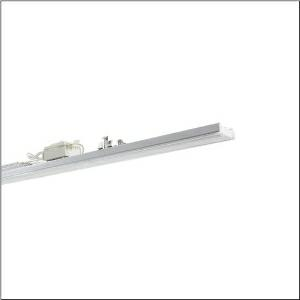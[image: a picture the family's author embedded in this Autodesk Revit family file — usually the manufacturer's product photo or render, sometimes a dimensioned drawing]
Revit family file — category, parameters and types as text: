
# Revit family: licross_11_recessed_ho_51tl12dn4exm
name_source: partatom
category: Lighting Fixtures
units: mm (PartAtom-declared; Revit-internal decimal feet)

## family parameters
Cut with Voids When Loaded = No
Host = Face
Light Source = No
Part Type = Normal
Room Calculation Point = No
Round Connector Dimension = Use Diameter
Shared = No

## types (1)
- --- (1 x LED, 14030 lm, 76.8 W, 4000K)
    Apparent Load = 77 VA
    CIE Flux Codes = 66 91 98 100 100
    Color Rendering = 80
    Color Temperature = 4000K
    Default Elevation = 1800 mm
    Description = Licross 11 Recessed HO, luminaire insert, of sheet steel, coil coated, white, length: 1.500mm, width: 66mm, height: 67mm, LED rated luminous flux: 14.030lm, light colour: 840, SDCM (Standard Deviation of Colour Matching)MacAdam ≤ 2 SDCM (initial), control gear: DALI 2, with plug, 5-pole, with phase selection, mains connection: 220..240V, AC, 50/60Hz, rated input power: 77W, internal wiring halogen-free, primary optical cover: cover, of PMMA, light emission: direct distribution, primary light characteristic: symmetric, protection rating (complete): IP40, insulation class (complete): insulation class I (protective earthing), certification: CE, ENEC, VDE, UKCA, protection symbol: D if used in an environment without relevant dust loads with corresponding accessories, impact resistance: IK06, permissible ambient temperature for indoor applications: -25..+30°C, corresponds to IFS (International Featured Standards) requirements for safety and quality in the food industry, reducing of maximum allowable ambient temperature of 5°C with ceiling mounting, LABS conformity tested according to VDMA 24364:2018-05, The light source and the operating device comply with the requirements of the Ecodesign Regulation (EU) 2019/2020 and are replaceable in accordance with this regulation, packaging unit: 1 piece
    Height = 58 mm
    Lamp = 1 x LED
    Lamp Light Flux = 14030 lm
    Lamp Power = 76.8 W
    Lamp count = 1
    Length = 1500 mm
    Luminous efficacy = 183 lm/W
    Manufacturer = Siteco
    ModVariant = No
    Model = 51TL12DN4EXM
    Mounting Place = Ceiling
    Mounting Type = Pendant
    Number of Poles = 1
    OnlyDefault = Yes
    Power Factor = 1
    Product Name = Licross 11 Recessed HO
    Product group = luminaire insert | ceiling pendant
    ProductGroupID = 901
    Protection Class = Protection class I
    Protection Degree = IP 40
    RLX_Detail_Level = 1
    RLX_Emergency_Light_Flux = 0 lm
    RLX_Emergency_Type = 0
    RLX_Emergency_Type_DB = No
    RlxData = <blob elided: 24881 chars, md5=6a829417>
    Socket = socket
    Standby Power = 0 W
    System Light Flux = 14030 lm
    System Power = 77 W
    Type Comments = factory setting: luminous flux: 100 % | dim-lin: 254 | 522 mA
    Type Image = l_1296930.jpg
    URL = http://relux.com
    VarID = @adj_030333
    Voltage = 0 V
    Weight = 0.00 kg
    Width = 66 mm

## geometry (parser evidence)
native form markers: Blend x4, Sweep x10
no freeform markers — native parametric forms only
